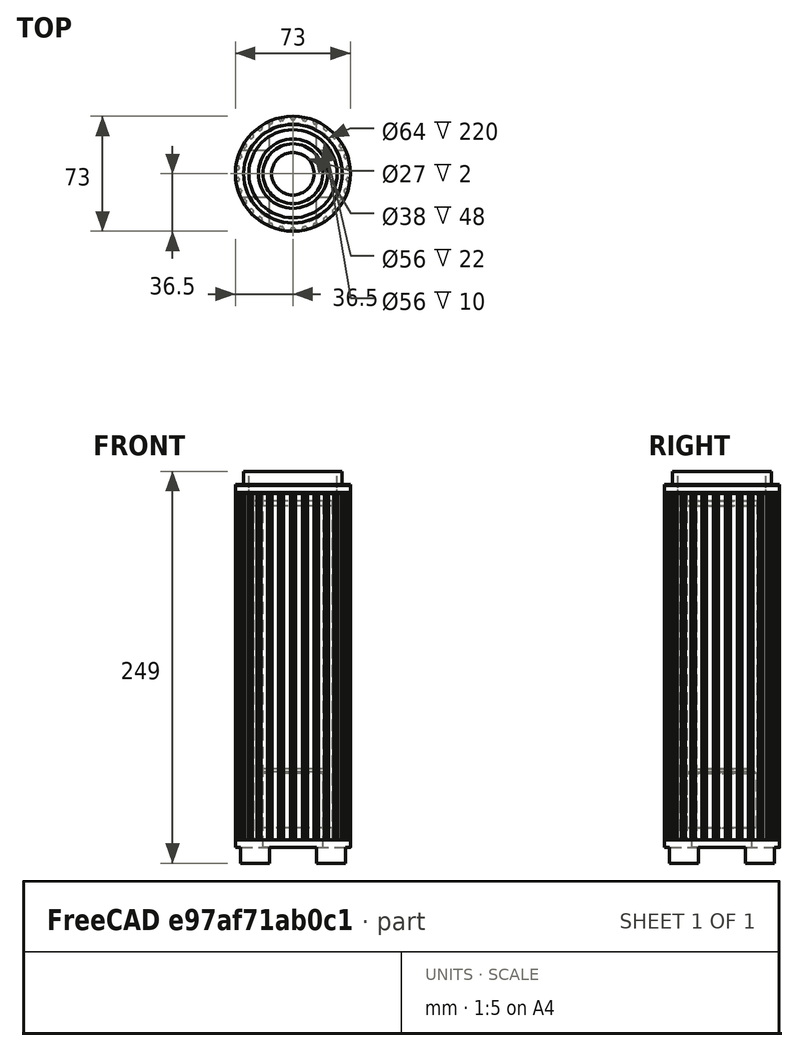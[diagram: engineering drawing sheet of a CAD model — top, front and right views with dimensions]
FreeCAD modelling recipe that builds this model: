
FCSTD DOCUMENT  (FreeCAD 0.15R4671 (Git))
Label: pica-small-v5
License: All rights reserved
LicenseURL: http://en.wikipedia.org/wiki/All_rights_reserved
objects: Part::Cylinder×14, Drawing::FeatureView×10, Part::Cut×7, Part::MultiFuse×6, Drawing::FeatureViewPart×6, Part::Box×2, Part::Part2DObjectPython×1, PartDesign::Pad×1, Drawing::FeaturePage×1, Part::Chamfer×1
note: 33 computed .brp shape members not serialized (recipe doc carries the construction recipe); baked Part::Feature solids carry a one-line shape summary decoded from their .brp

FEATURE [Part::Part2DObjectPython] InvoluteGear  # Draft 2D object (typed FeaturePython)
  ExternalGear = true
  HighPrecision = true
  Modules = 2.5
  NumberOfTeeth = 30
  PressureAngle = 20
FEATURE [PartDesign::Pad] Pad
  Length = 220
  Length2 = 100
  Sketch = -> InvoluteGear
  Type = 0
FEATURE [Part::Cylinder] Cylinder
  Angle = 360
  Height = 240
  Placement = pos=(0,0,-10) rot=(0,0,1;0rad)
  Radius = 32
FEATURE [Part::Cut] Cut  label="Final"
  Base = -> Pad
  Tool = -> Cylinder
FEATURE [Part::Cylinder] Cylinder001
  Angle = 360
  Height = 400
  Radius = 36.5
FEATURE [Part::Cylinder] Cylinder002
  Angle = 360
  Height = 400
  Radius = 100
FEATURE [Part::Cut] Cut001
  Base = -> Cylinder002
  Tool = -> Cylinder001
FEATURE [Part::Cut] Cut002  label="Shade"
  Base = -> Cut
  Placement = pos=(0,0,15) rot=(0,0,1;0rad)
  Tool = -> Cut001
FEATURE [Part::Cylinder] Cylinder003
  Angle = 360
  Height = 15
  Radius = 36.5
FEATURE [Part::Cylinder] Cylinder004
  Angle = 360
  Height = 22.5
  Radius = 31.3
FEATURE [Part::MultiFuse] Fusion  label="Base Fusion"
  Shapes = -> [Cylinder004,Cylinder003]
FEATURE [Drawing::FeatureViewPart] FrontView  label="Shade Side"
  Direction = (0,-1,0)
  HiddenWidth = 0.15
  LineWidth = 0.35
  Rotation = 90
  ShowHiddenLines = true
  ShowSmoothLines = false
  Source = -> Cut002
  Tolerance = 0.05
  ViewResult = <blob: 104580 chars omitted>
  Visible = true
  X = 80
  Y = 270
FEATURE [Drawing::FeatureViewPart] View001  label="Shade Top"
  Direction = (0,0,1)
  HiddenWidth = 0.15
  LineWidth = 0.35
  Rotation = 0
  ShowHiddenLines = false
  ShowSmoothLines = false
  Source = -> Cut002
  Tolerance = 0.05
  ViewResult = <blob: 17331 chars omitted>
  Visible = true
  X = 300
  Y = 80
FEATURE [Drawing::FeatureView] dim006  label="Base Radius"
  Rotation = 0
  ViewResult = <g   >\n <circle cx ="300.000000" cy ="170.000000" r="0.500000" stroke="none" fill="rgb(0,0,0)" /> \n<line x1="255.718312" y1="135.631286" x2="300.000000" y2="170.000000" style="stroke:rgb(0,0,0);stroke-width:0.30" />\n<polygon points="275.273643,150.808927 277.030448,153.438307 278.433561,153.261461 278.256715,151.858348" style="fill:rgb(0,0,0);stroke:rgb(0,0,0);stroke-width:0" />\n<line x1="255.718312" y1="135.631286" x2="231.639949" y2="135.631286" style="stroke:rgb(0,0,0);stroke-width:0.30" />\n<text x="219.448373" y="136.850443" font-family="Arial" font-size="3.6" fill="rgb(0,0,0)" text-anchor="inherit"  >R31.3</text>\n<!--31.3-->\n<!--R%3.3f-->\n</g> 
  Visible = true
  X = 0
  Y = 0
FEATURE [Drawing::FeatureView] centerLines
  Rotation = 0
  ViewResult = <g  transform="scale(1.000000,1.000000)" stroke="rgb(0,0,0)"  stroke-width="0.300000" >\n<path d="M 300.000000,170.000000 L 300.000000,168.000000 M 300.000000,166.000000 L 300.000000,160.000000 M 300.000000,158.000000 L 300.000000,156.000000 "/>\n<path d="M 300.000000,170.000000 L 302.000000,170.000000 M 304.000000,170.000000 L 310.000000,170.000000 M 312.000000,170.000000 L 314.000000,170.000000 "/>\n<path d="M 300.000000,170.000000 L 300.000000,172.000000 M 300.000000,174.000000 L 300.000000,180.000000 M 300.000000,182.000000 L 300.000000,184.000000 "/>\n<path d="M 300.000000,170.000000 L 298.000000,170.000000 M 296.000000,170.000000 L 290.000000,170.000000 M 288.000000,170.000000 L 286.000000,170.000000 "/>\n</g> 
  Visible = true
  X = 0
  Y = 0
FEATURE [Drawing::FeatureView] centerLines001
  Rotation = 0
  ViewResult = <g  transform="scale(1.000000,1.000000)" stroke="rgb(0,0,0)"  stroke-width="0.300000" >\n<path d="M 300.000000,80.000000 L 300.000000,82.000000 M 300.000000,84.000000 L 300.000000,90.000000 M 300.000000,92.000000 L 300.000000,94.000000 "/>\n<path d="M 300.000000,80.000000 L 302.000000,80.000000 M 304.000000,80.000000 L 310.000000,80.000000 M 312.000000,80.000000 L 314.000000,80.000000 "/>\n<path d="M 300.000000,80.000000 L 300.000000,78.000000 M 300.000000,76.000000 L 300.000000,70.000000 M 300.000000,68.000000 L 300.000000,66.000000 "/>\n<path d="M 300.000000,80.000000 L 298.000000,80.000000 M 296.000000,80.000000 L 290.000000,80.000000 M 288.000000,80.000000 L 286.000000,80.000000 "/>\n</g> 
  Visible = true
  X = 0
  Y = 0
FEATURE [Drawing::FeatureView] dim007  label="Shade Radius"
  Rotation = 0
  ViewResult = <g   >\n <circle cx ="300.000000" cy ="80.000000" r="0.500000" stroke="none" fill="rgb(0,0,0)" /> \n<line x1="340.917441" y1="111.884102" x2="300.000000" y2="80.000000" style="stroke:rgb(0,0,0);stroke-width:0.30" />\n<polygon points="325.241495,99.668933 323.489759,97.036174 322.086308,97.210316 322.260451,98.613767" style="fill:rgb(0,0,0);stroke:rgb(0,0,0);stroke-width:0" />\n<line x1="340.917441" y1="111.884102" x2="365.557939" y2="111.884102" style="stroke:rgb(0,0,0);stroke-width:0.30" />\n<text x="369.473360" y="112.835313" font-family="Arial" font-size="3.6" fill="rgb(0,0,0)" text-anchor="inherit"  >R32</text>\n<!--32.0-->\n<!--R%3.3f-->\n</g> 
  Visible = true
  X = 0
  Y = 0
FEATURE [Part::Cylinder] Cylinder005
  Angle = 360
  Height = 90
  Radius = 13.5
FEATURE [Part::Cylinder] Cylinder006
  Angle = 360
  Height = 58
  Radius = 19
FEATURE [Part::MultiFuse] Fusion002  label="Fixture Mount"
  Shapes = -> [Cylinder005,Cylinder006]
FEATURE [Drawing::FeatureViewPart] View004  label="Base Top"
  Direction = (0,0,1)
  HiddenWidth = 0.15
  LineWidth = 0.35
  Rotation = 0
  ShowHiddenLines = false
  ShowSmoothLines = false
  Tolerance = 0.05
  ViewResult = <g id="Base Top"\n   transform="rotate(0,300,170) translate(300,170) scale(1,1)"\n  >\n<g   stroke="rgb(0, 0, 0)"\n   stroke-width="0.35"\n   stroke-linecap="butt"\n   stroke-linejoin="miter"\n   fill="none"\n   transform="scale(1,-1)"\n  >\n<circle cx ="0" cy ="0" r ="23.3" /><circle cx ="0" cy ="0" r ="15" /><circle cx ="0" cy ="0" r ="31.3" /><circle cx ="0" cy ="0" r ="36.5" /></g>\n</g>
  Visible = true
  X = 300
  Y = 170
FEATURE [Drawing::FeatureViewPart] View005  label="Base Side"
  Direction = (0,-1,0)
  HiddenWidth = 0.15
  LineWidth = 0.35
  Rotation = 90
  ShowHiddenLines = false
  ShowSmoothLines = false
  Tolerance = 0.05
  ViewResult = <blob: 2600 chars omitted>
  Visible = true
  X = 80
  Y = 270
FEATURE [Drawing::FeatureViewPart] View  label="Base Side001"
  Direction = (0,-1,0)
  HiddenWidth = 0.15
  LineWidth = 0.35
  Rotation = 90
  ShowHiddenLines = false
  ShowSmoothLines = false
  Tolerance = 0.05
  ViewResult = <blob: 2605 chars omitted>
  Visible = true
  X = 180
  Y = 100
FEATURE [Drawing::FeatureViewPart] View006  label="Base Top001"
  Direction = (0,0,-1)
  HiddenWidth = 0.15
  LineWidth = 0.35
  Rotation = 0
  ShowHiddenLines = false
  ShowSmoothLines = false
  Tolerance = 0.05
  ViewResult = <blob: 2659 chars omitted>
  Visible = true
  X = 180
  Y = 170
FEATURE [Drawing::FeatureView] dim010  label="dim001"
  Rotation = 0
  ViewResult = <g   >\n<line x1="158.500000" y1="235.000000" x2="177.679727" y2="235.000000" style="stroke:rgb(0,0,0);stroke-width:0.30" />\n<line x1="158.483300" y1="250.000000" x2="177.679727" y2="250.000000" style="stroke:rgb(0,0,0);stroke-width:0.30" />\n<line x1="176.679727" y1="235.000000" x2="176.679727" y2="250.000000" style="stroke:rgb(0,0,0);stroke-width:0.30" />\n<polygon points="176.679727,235.000000 175.679727,238.000000 176.679727,239.000000 177.679727,238.000000" style="fill:rgb(0,0,0);stroke:rgb(0,0,0);stroke-width:0" /><polygon points="176.679727,250.000000 177.679727,247.000000 176.679727,246.000000 175.679727,247.000000" style="fill:rgb(0,0,0);stroke:rgb(0,0,0);stroke-width:0" />\n<text x="183.587709" y="244.783611" font-family="Arial" font-size="3.6" fill="rgb(0,0,0)" text-anchor="inherit" transform="rotate(-90.000000 183.587709,244.783611)" >15</text>\n</g> 
  Visible = true
  X = 0
  Y = 0
FEATURE [Drawing::FeatureView] dim011  label="dim002"
  Rotation = 0
  ViewResult = <g   >\n<line x1="153.300000" y1="228.000000" x2="177.810311" y2="228.000000" style="stroke:rgb(0,0,0);stroke-width:0.30" />\n<line x1="158.500000" y1="235.000000" x2="177.810311" y2="235.000000" style="stroke:rgb(0,0,0);stroke-width:0.30" />\n<line x1="176.810311" y1="228.000000" x2="176.810311" y2="235.000000" style="stroke:rgb(0,0,0);stroke-width:0.30" />\n<polygon points="176.810311,228.000000 177.810311,225.000000 176.810311,224.000000 175.810311,225.000000" style="fill:rgb(0,0,0);stroke:rgb(0,0,0);stroke-width:0" /><polygon points="176.810311,235.000000 175.810311,238.000000 176.810311,239.000000 177.810311,238.000000" style="fill:rgb(0,0,0);stroke:rgb(0,0,0);stroke-width:0" />\n<text x="183.208911" y="232.569545" font-family="Arial" font-size="3.6" fill="rgb(0,0,0)" text-anchor="inherit" transform="rotate(-90.000000 183.208911,232.569545)" >7</text>\n</g> 
  Visible = true
  X = 0
  Y = 0
FEATURE [Drawing::FeatureView] centerLines004
  Rotation = 0
  ViewResult = <g  transform="scale(1.000000,1.000000)" stroke="rgb(0,0,0)"  stroke-width="0.300000" >\n<path d="M 180.000000,169.999925 L 180.000000,167.999925 M 180.000000,165.999925 L 180.000000,159.999925 M 180.000000,157.999925 L 180.000000,155.999925 "/>\n<path d="M 180.000000,169.999925 L 182.000000,169.999925 M 184.000000,169.999925 L 190.000000,169.999925 M 192.000000,169.999925 L 194.000000,169.999925 "/>\n<path d="M 180.000000,169.999925 L 180.000000,171.999925 M 180.000000,173.999925 L 180.000000,179.999925 M 180.000000,181.999925 L 180.000000,183.999925 M 180.000000,185.999925 L 180.000000,186.160469 "/>\n<path d="M 180.000000,169.999925 L 178.000000,169.999925 M 176.000000,169.999925 L 170.000000,169.999925 M 168.000000,169.999925 L 166.583365,169.999925 "/>\n</g> 
  Visible = true
  X = 0
  Y = 0
FEATURE [Drawing::FeatureView] dim
  Rotation = 0
  ViewResult = <g   >\n<line x1="41.500000" y1="25.000000" x2="33.944194" y2="25.000000" style="stroke:rgb(0,0,0);stroke-width:0.30" />\n<line x1="41.500000" y1="245.000000" x2="33.944194" y2="245.000000" style="stroke:rgb(0,0,0);stroke-width:0.30" />\n<line x1="34.944194" y1="25.000000" x2="34.944194" y2="245.000000" style="stroke:rgb(0,0,0);stroke-width:0.30" />\n<polygon points="34.944194,25.000000 33.944194,28.000000 34.944194,29.000000 35.944194,28.000000" style="fill:rgb(0,0,0);stroke:rgb(0,0,0);stroke-width:0" /><polygon points="34.944194,245.000000 35.944194,242.000000 34.944194,241.000000 33.944194,242.000000" style="fill:rgb(0,0,0);stroke:rgb(0,0,0);stroke-width:0" />\n<text x="31.608126" y="136.256650" font-family="Arial" font-size="3.6" fill="rgb(0,0,0)" text-anchor="inherit" transform="rotate(-90.000000 31.608126,136.256650)" >220</text>\n</g> 
  Visible = true
  X = 0
  Y = 0
FEATURE [Drawing::FeatureView] dim012
  Rotation = 0
  ViewResult = <g   >\n<line x1="118.122400" y1="245.000000" x2="126.861722" y2="245.000000" style="stroke:rgb(0,0,0);stroke-width:0.30" />\n<line x1="115.275400" y1="270.000000" x2="126.861722" y2="270.000000" style="stroke:rgb(0,0,0);stroke-width:0.30" />\n<line x1="125.861722" y1="245.000000" x2="125.861722" y2="270.000000" style="stroke:rgb(0,0,0);stroke-width:0.30" />\n<polygon points="125.861722,245.000000 124.861722,248.000000 125.861722,249.000000 126.861722,248.000000" style="fill:rgb(0,0,0);stroke:rgb(0,0,0);stroke-width:0" /><polygon points="125.861722,270.000000 126.861722,267.000000 125.861722,266.000000 124.861722,267.000000" style="fill:rgb(0,0,0);stroke:rgb(0,0,0);stroke-width:0" />\n<text x="132.056471" y="260.197520" font-family="Arial" font-size="3.6" fill="rgb(0,0,0)" text-anchor="inherit" transform="rotate(-90.000000 132.056471,260.197520)" >25</text>\n</g> 
  Visible = true
  X = 0
  Y = 0
FEATURE [Drawing::FeatureView] dim013
  Rotation = 0
  ViewResult = <g   >\n<line x1="143.500000" y1="73.000000" x2="143.500000" y2="45.465562" style="stroke:rgb(0,0,0);stroke-width:0.30" />\n<line x1="216.500000" y1="73.000000" x2="216.500000" y2="45.465562" style="stroke:rgb(0,0,0);stroke-width:0.30" />\n<line x1="143.500000" y1="46.465562" x2="216.500000" y2="46.465562" style="stroke:rgb(0,0,0);stroke-width:0.30" />\n<polygon points="143.500000,46.465562 146.500000,47.465562 147.500000,46.465562 146.500000,45.465562" style="fill:rgb(0,0,0);stroke:rgb(0,0,0);stroke-width:0" /><polygon points="216.500000,46.465562 213.500000,45.465562 212.500000,46.465562 213.500000,47.465562" style="fill:rgb(0,0,0);stroke:rgb(0,0,0);stroke-width:0" />\n<text x="177.413963" y="43.541156" font-family="Arial" font-size="3.6" fill="rgb(0,0,0)" text-anchor="inherit" transform="rotate(0.000000 177.413963,43.541156)" >73</text>\n</g> 
  Visible = true
  X = 0
  Y = 0
FEATURE [Drawing::FeaturePage] AutoDrawing  label="Initial Sketch"
  EditableTexts = FLOYD DIEBEL | 8/22/2015 | 1:1 | 1 | 1 | PICA (SMALL V2) | LAMP WITH SHADE
  Group = -> [FrontView,View001,dim006,centerLines,centerLines001,dim007,View004,View005,dim010,dim011,View,View006,centerLines004,dim,dim012,dim013]
  Template = C:/Program Files/FreeCAD 0.15/data/Mod/Drawing/Templates/A3_Landscape.svg
FEATURE [Part::Cylinder] Cylinder007
  Angle = 360
  Height = 60
  Radius = 22
FEATURE [Part::MultiFuse] Fusion003
  Shapes = -> [Fusion,Cylinder007]
FEATURE [Part::Cut] Cut005  label="Raw"
  Base = -> Fusion003
  Tool = -> Fusion002
FEATURE [Part::Box] Box002  label="Cube002"
  Height = 10
  Length = 100
  Placement = pos=(-50,-15,0) rot=(0,0,1;0rad)
  Width = 30
FEATURE [Part::Box] Box003  label="Cube003"
  Height = 10
  Length = 100
  Placement = pos=(15,-50,0) rot=(0,0,1;1.5708rad)
  Width = 30
FEATURE [Part::MultiFuse] Fusion004  label="Feet Cutout Fusion001"
  Shapes = -> [Box003,Box002]
FEATURE [Part::Cut] Cut006  label="Pre-chamfer"
  Base = -> Cut005
  Tool = -> Fusion004
FEATURE [Part::Chamfer] Chamfer  label="Base"
  Base = -> Cut006
  Edges = 1 edges r=3: [Edge1]
FEATURE [Part::Cylinder] Cylinder008
  Angle = 360
  Height = 5
  Placement = pos=(0,0,8.5) rot=(0,0,1;0rad)
  Radius = 36.5
FEATURE [Part::Cylinder] Cylinder009
  Angle = 360
  Height = 22
  Radius = 31.3
FEATURE [Part::MultiFuse] Fusion005  label="No Cutout"
  Shapes = -> [Cylinder009,Cylinder008]
FEATURE [Part::Cylinder] Cylinder010
  Angle = 360
  Height = 55
  Placement = pos=(0,0,-10) rot=(0,0,1;0rad)
  Radius = 28
FEATURE [Part::Cut] Cut007  label="Joint"
  Base = -> Fusion005
  Placement = pos=(0,0,227) rot=(0,0,1;0rad)
  Tool = -> Cylinder010
FEATURE [Part::Cylinder] Cylinder011
  Angle = 360
  Height = 5
  Placement = pos=(0,0,5) rot=(0,0,1;0rad)
  Radius = 36.5
FEATURE [Part::Cylinder] Cylinder012
  Angle = 360
  Height = 10
  Radius = 31.3
FEATURE [Part::MultiFuse] Fusion006  label="No Cutout001"
  Shapes = -> [Cylinder012,Cylinder011]
FEATURE [Part::Cylinder] Cylinder013
  Angle = 360
  Height = 55
  Placement = pos=(0,0,-10) rot=(0,0,1;0rad)
  Radius = 28
FEATURE [Part::Cut] Cut008  label="Cap"
  Base = -> Fusion006
  Placement = pos=(0,0,230) rot=(0,0,1;0rad)
  Tool = -> Cylinder013
